# Revit family: HERZ Ball valve with T-handle (silumin) 2211
name_source: partatom
category: Rohrzubehör
units: mm (PartAtom-declared; Revit-internal decimal feet)

## family parameters
Arbeitsebenenbasiert = Nein
Beim Laden mit Abzugskörper schneiden = Nein
Bemaßung runder Anschluss = Durchmesser verwenden
Gemeinsam genutzt = Nein
Immer vertikal = Ja
OmniClass-Nummer = 23.65.55.14
OmniClass-Titel = Valves for Liquid Services
Teiletyp = Unterbricht

## types (1)
- HERZ Ball valve with T-handle (silumin) 2211
    Application = HERZ ball valve MODUL is designed for building services such as heating and chilled water plants.
The operating conditions (temperature, pressure) should be constant.
    Ball = forged brass according to EN 12165, hollow, full bore, hard chrome plated, CW617N
    Ball seals = PTFE
    Body = forged brass according to EN 12165, nickel plated, CW617N
    External threaded connectors = according to ISO 7-1
    Field of application = HERZ ball valves have to be used as shut off elements.
Field of application are building services, such as heating or chilled water plants.
Ball valves are used wherever the medium flow has to be reliably closed.
Ball valve should not be used as regulating element so it has to be fully opened or fully closed (the handle should not be in intermediate position).
    Handle = T-handle, red, silumin
    Hersteller = HERZ Armaturen Ges.m.b.H
    Internal threaded connectors = according to ISO 228-1
    Max. operating pressure = 2500000.0 Pa
    Max. operating pressure (screw connection) = 1600000.0 Pa
    Max. operating temperature = 150 °C
    Max. operating temperature (water - no steam) = 110 °C
    Medium = Heating water quality according to ÖNORM H5195 or VDI-Standard 2035.
The use of ethylene or propylene glycol in a mixing ratio 25- 50% is allowed.
    Min. operating temperature = -30 °C
    Min. operating temperature (water) = 1 °C
    S03 = 10 mm  [stored 0.0328084 ft]
    SCRNCODE = 05;10;02
    SCRNSEQ = ARM;ARM_TYP="ABVS";2
    Seals (screw connection) DN15-DN25 = EPDM (O-Ring)
    Seals (screw connection) DN32-DN50 = KLINGER (flat sealing)
    Spindle = machined brass according to EN 12164, CW614N
    Spindle seals = PTFE
    URL = www.herzvalves.com
    Vorgabe-Ansicht = 0 mm  [stored 0 ft]
    W01 = 135.00°

note: [stored X ft] marks values corroborated as IEEE doubles in the binary element streams (Revit-internal decimal feet)
